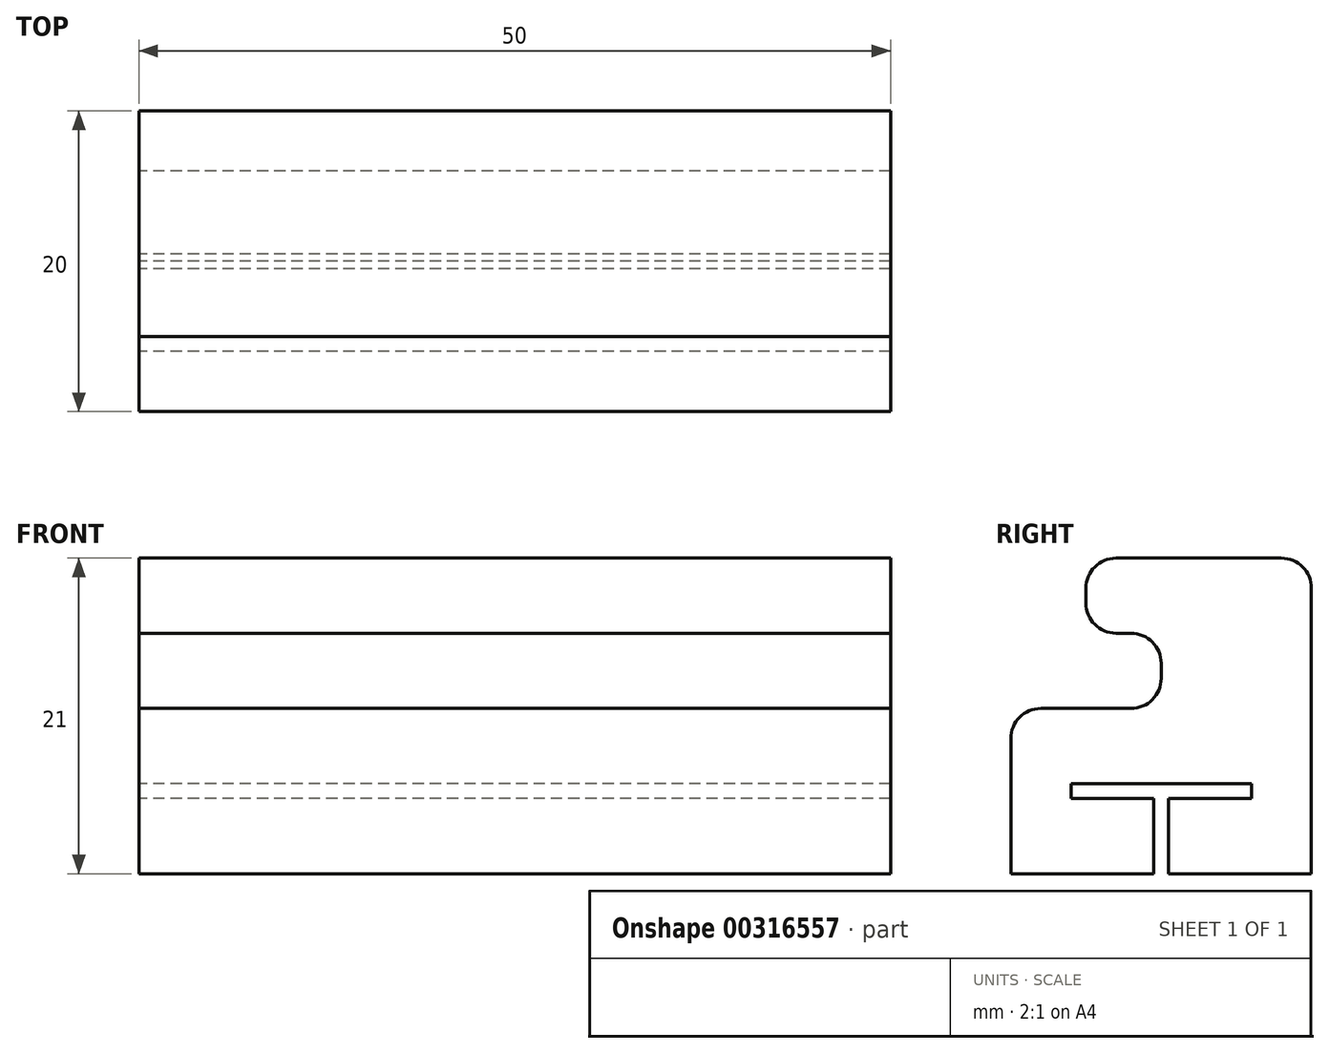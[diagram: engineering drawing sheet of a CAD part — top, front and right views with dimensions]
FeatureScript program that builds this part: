
annotation { "Feature Type Name" : "Feature", "Feature Type Description" : "" }
export const myFeature = defineFeature(function(context is Context, id is Id, definition is map)
    precondition{}
    {
        {
            var Q0;
            Q0=qCreatedBy(makeId("Right.planeOp"),FACE);
            var sketch = newSketch(context, id + "F0", { "sketchPlane" : qUnion([Q0])});
            skLineSegment(sketch, "E0", {"start": v(10, 0) * mm, "end": v(10, 19) * mm});
            skLineSegment(sketch, "E1", {"start": v(8, 21) * mm, "end": v(-3, 21) * mm});
            skLineSegment(sketch, "E2", {"start": v(-5, 19) * mm, "end": v(-5, 18) * mm});
            skLineSegment(sketch, "E3", {"start": v(-3, 16) * mm, "end": v(-2, 16) * mm});
            skLineSegment(sketch, "E4", {"start": v(0, 14) * mm, "end": v(0, 13) * mm});
            skLineSegment(sketch, "E5", {"start": v(-2, 11) * mm, "end": v(-8, 11) * mm});
            skLineSegment(sketch, "E6", {"start": v(-10, 9) * mm, "end": v(-10, 0) * mm});
            skLineSegment(sketch, "E7", {"start": v(-10, 0) * mm, "end": v(-0.5, 0) * mm});
            skLineSegment(sketch, "E8", {"start": v(-0.5, 0) * mm, "end": v(-0.5, 5) * mm});
            skLineSegment(sketch, "E9", {"start": v(-0.5, 5) * mm, "end": v(-6, 5) * mm});
            skLineSegment(sketch, "E10", {"start": v(-6, 5) * mm, "end": v(-6, 6) * mm});
            skLineSegment(sketch, "E11", {"start": v(-6, 6) * mm, "end": v(6, 6) * mm});
            skLineSegment(sketch, "E12", {"start": v(6, 6) * mm, "end": v(6, 5) * mm});
            skLineSegment(sketch, "E13", {"start": v(6, 5) * mm, "end": v(0.5, 5) * mm});
            skLineSegment(sketch, "E14", {"start": v(0.5, 5) * mm, "end": v(0.5, 0) * mm});
            skLineSegment(sketch, "E15", {"start": v(0.5, 0) * mm, "end": v(10, 0) * mm});
            skPoint(sketch, "E16.visualSharp", {"position": v(-5, 21) * mm});
            skArc(sketch, "E16.filletArc", {"start": v(-3, 21) * mm, "mid": v(-4.41, 20.41) * mm, "end": v(-5, 19) * mm});
            skPoint(sketch, "E17.visualSharp", {"position": v(-5, 16) * mm});
            skArc(sketch, "E17.filletArc", {"start": v(-5, 18) * mm, "mid": v(-4.41, 16.59) * mm, "end": v(-3, 16) * mm});
            skPoint(sketch, "E18.visualSharp", {"position": v(0, 16) * mm});
            skArc(sketch, "E18.filletArc", {"start": v(0, 14) * mm, "mid": v(-0.59, 15.41) * mm, "end": v(-2, 16) * mm});
            skPoint(sketch, "E19.visualSharp", {"position": v(-10, 11) * mm});
            skArc(sketch, "E19.filletArc", {"start": v(-8, 11) * mm, "mid": v(-9.41, 10.41) * mm, "end": v(-10, 9) * mm});
            skPoint(sketch, "E20.visualSharp", {"position": v(10, 21) * mm});
            skArc(sketch, "E20.filletArc", {"start": v(10, 19) * mm, "mid": v(9.41, 20.41) * mm, "end": v(8, 21) * mm});
            skPoint(sketch, "E21.visualSharp", {"position": v(0, 11) * mm});
            skArc(sketch, "E21.filletArc", {"start": v(-2, 11) * mm, "mid": v(-0.59, 11.59) * mm, "end": v(0, 13) * mm});
            skSolve(sketch);
        }
        {
            var Q0;
            Q0=makeQuery(id+"F0.imprint","IMPRINT",FACE,{"disambiguationData":[TD([[makeQuery(id+"F0.imprint","IMPRINT",EDGE,{"derivedFrom":sQuery(id+"F0.wireOp",EDGE,"E0")}),1.0]])]});
            extrude(context, id + "F1", {"entities" : qUnion([Q0]), "endBound" : BoundingType.SYMMETRIC, "depth" : 50 * mm});
        }
    });
